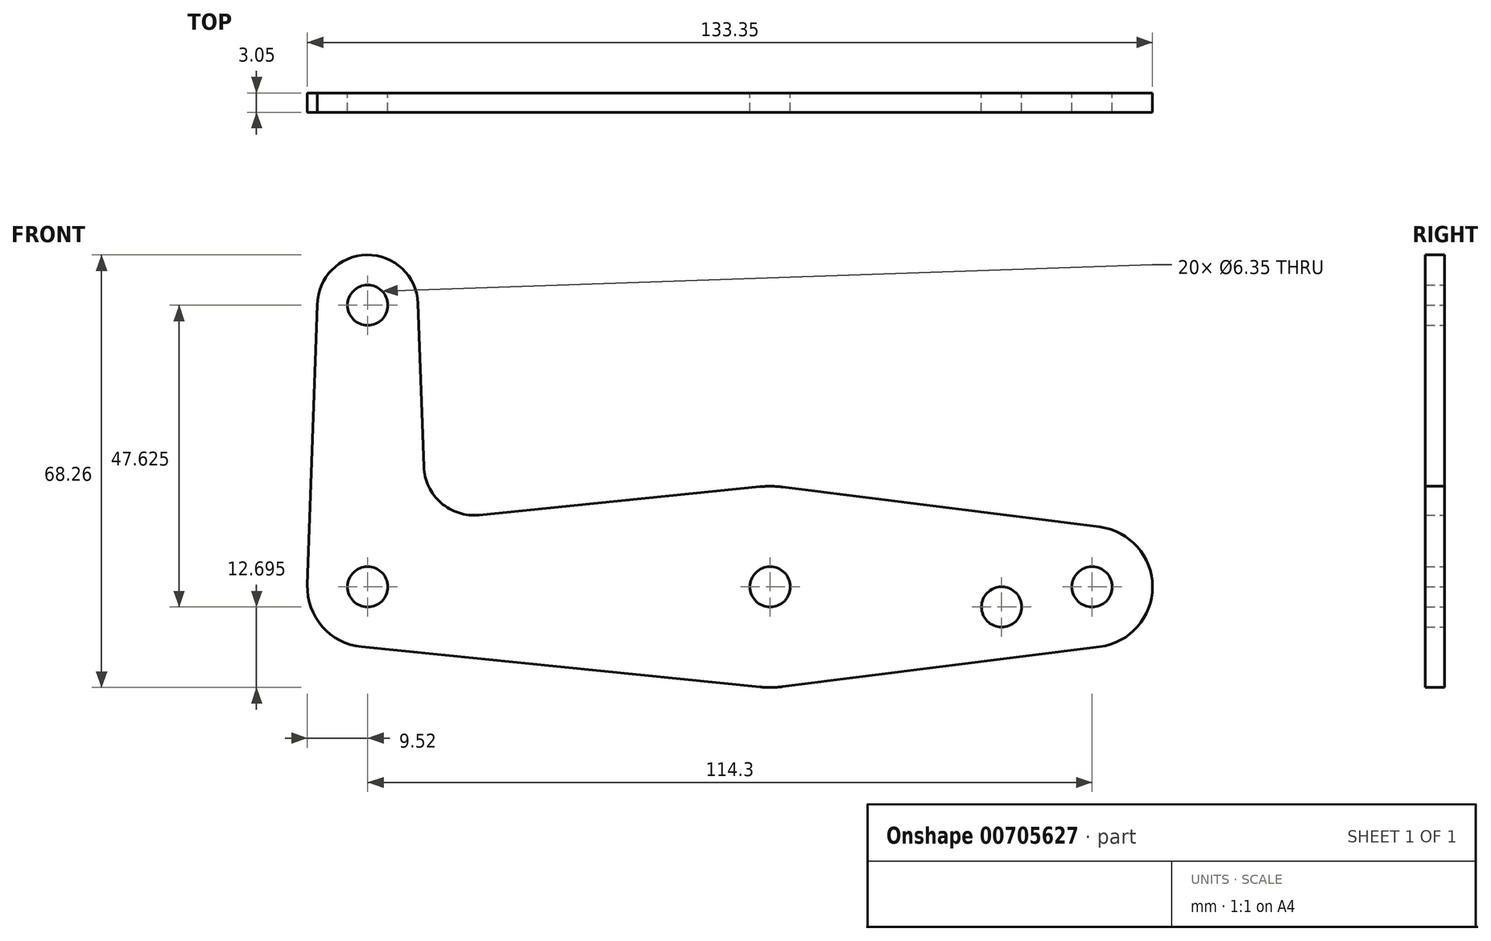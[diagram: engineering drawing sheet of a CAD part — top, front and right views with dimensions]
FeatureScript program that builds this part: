
annotation { "Feature Type Name" : "Feature", "Feature Type Description" : "" }
export const myFeature = defineFeature(function(context is Context, id is Id, definition is map)
    precondition{}
    {
        {
            var Q0;
            Q0=qCreatedBy(makeId("Front.planeOp"),FACE);
            var sketch = newSketch(context, id + "F0", { "sketchPlane" : qUnion([Q0])});
            skCircle(sketch, "E0", {"center": v(0, 0) * mm, "radius": 9.53 * mm});
            skLineSegment(sketch, "E1", {"start": v(0, 0) * mm, "end": v(0, 44.45) * mm, "construction": true});
            skCircle(sketch, "E2", {"center": v(0, 44.45) * mm, "radius": 7.94 * mm});
            skLineSegment(sketch, "E3", {"start": v(0, 0) * mm, "end": v(114.3, 0) * mm, "construction": true});
            skCircle(sketch, "E4", {"center": v(114.3, 0) * mm, "radius": 9.53 * mm});
            skCircle(sketch, "E5", {"center": v(63.5, 0) * mm, "radius": 15.88 * mm});
            skLineSegment(sketch, "E6", {"start": v(-7.94, 44.45) * mm, "end": v(-9.53, 0) * mm});
            skCircle(sketch, "E7", {"center": v(0, 44.45) * mm, "radius": 3.18 * mm});
            skCircle(sketch, "E8", {"center": v(0, 0) * mm, "radius": 3.18 * mm});
            skCircle(sketch, "E9", {"center": v(63.5, 0) * mm, "radius": 3.18 * mm});
            skCircle(sketch, "E10", {"center": v(114.3, 0) * mm, "radius": 3.18 * mm});
            skCircle(sketch, "E11", {"center": v(100.03, -3.18) * mm, "radius": 3.18 * mm});
            skLineSegment(sketch, "E12", {"start": v(-0.95, -9.48) * mm, "end": v(61.91, -15.8) * mm});
            skLineSegment(sketch, "E13", {"start": v(115.5, -9.45) * mm, "end": v(65.48, -15.75) * mm});
            skLineSegment(sketch, "E14", {"start": v(7.93, 44.73) * mm, "end": v(8.85, 18.97) * mm});
            skLineSegment(sketch, "E15", {"start": v(17.6, 11.34) * mm, "end": v(61.91, 15.8) * mm});
            skLineSegment(sketch, "E16", {"start": v(115.5, 9.45) * mm, "end": v(65.48, 15.75) * mm});
            skArc(sketch, "E17.filletArc", {"start": v(8.85, 18.97) * mm, "mid": v(11.57, 13.26) * mm, "end": v(17.6, 11.34) * mm});
            skSolve(sketch);
        }
        {
            var Q0;
            Q0 = qSketchRegion(id + "F0", true);
            extrude(context, id + "F1", {"entities" : qUnion([Q0]), "depth" : 3.05 * mm, "offsetDistance" : 25.4 * mm});
        }
    });
